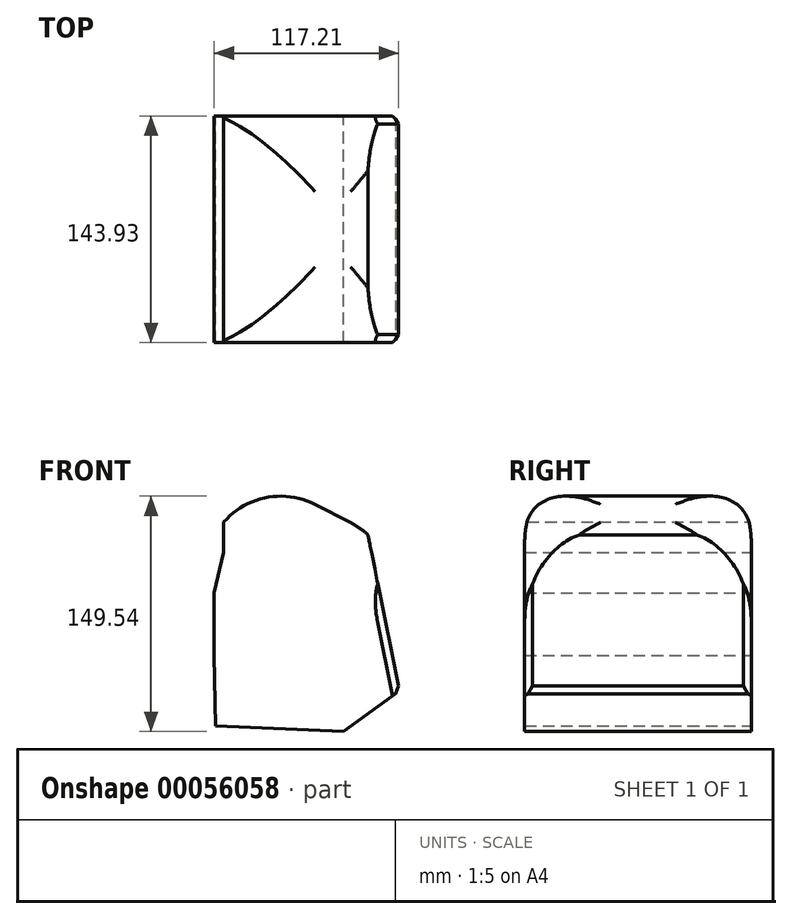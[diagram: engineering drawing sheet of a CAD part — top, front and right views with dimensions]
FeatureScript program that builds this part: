
annotation { "Feature Type Name" : "Feature", "Feature Type Description" : "" }
export const myFeature = defineFeature(function(context is Context, id is Id, definition is map)
    precondition{}
    {
        {
            var Q0;
            Q0=qCreatedBy(makeId("Front.planeOp"),FACE);
            var sketch = newSketch(context, id + "F0", { "sketchPlane" : qUnion([Q0])});
            skLineSegment(sketch, "E0", {"start": v(0, 114.28) * mm, "end": v(40.75, 193.9) * mm});
            skLineSegment(sketch, "E1", {"start": v(40.75, 193.9) * mm, "end": v(115.24, 155.79) * mm});
            skLineSegment(sketch, "E2", {"start": v(115.24, 155.79) * mm, "end": v(135.97, 54.13) * mm});
            skLineSegment(sketch, "E3", {"start": v(135.97, 54.13) * mm, "end": v(100.26, 28.42) * mm});
            skLineSegment(sketch, "E4", {"start": v(100.26, 28.42) * mm, "end": v(18.84, 32.07) * mm});
            skLineSegment(sketch, "E5", {"start": v(18.84, 32.07) * mm, "end": v(18.11, 76.73) * mm});
            skLineSegment(sketch, "E6", {"start": v(18.11, 76.73) * mm, "end": v(18.11, 116.29) * mm});
            skLineSegment(sketch, "E7", {"start": v(18.11, 116.29) * mm, "end": v(24.2, 142.01) * mm});
            skLineSegment(sketch, "E8", {"start": v(24.2, 142.01) * mm, "end": v(24.2, 161.59) * mm});
            skSolve(sketch);
        }
        {
            var Q0;
            {var subQ0=sQuery(id+"F0.wireOp",EDGE,"E1");Q0=makeQuery(id+"F0.imprint","IMPRINT",FACE,{"disambiguationData":[TD([[makeQuery(id+"F0.imprint","IMPRINT",EDGE,{"derivedFrom":subQ0}),-1.0]])]});}
            extrude(context, id + "F1", {"entities" : qUnion([Q0]), "depth" : 143.93 * mm, "offsetDistance" : 25 * mm});
        }
        {
            var Q0;
            Q0=makeQuery(id+"F1.opExtrude","SWEPT_FACE",FACE,{"disambiguationData":[OSD([sQuery(id+"F0.wireOp",EDGE,"E2")])]});
            chamfer(context, id + "F2", {"entities" : qUnion([Q0]), "width" : 5 * mm, "tangentPropagation" : true});
        }
        {
            var Q0;
            Q0=makeQuery(id+"F1.opExtrude","SWEPT_FACE",FACE,{"disambiguationData":[OSD([sQuery(id+"F0.wireOp",EDGE,"E1")])]});
            fillet(context, id + "F3", {"entities" : qUnion([Q0]), "radius" : 48.03 * mm, "tangentPropagation" : true, "allowEdgeOverflow" : false});
        }
    });
